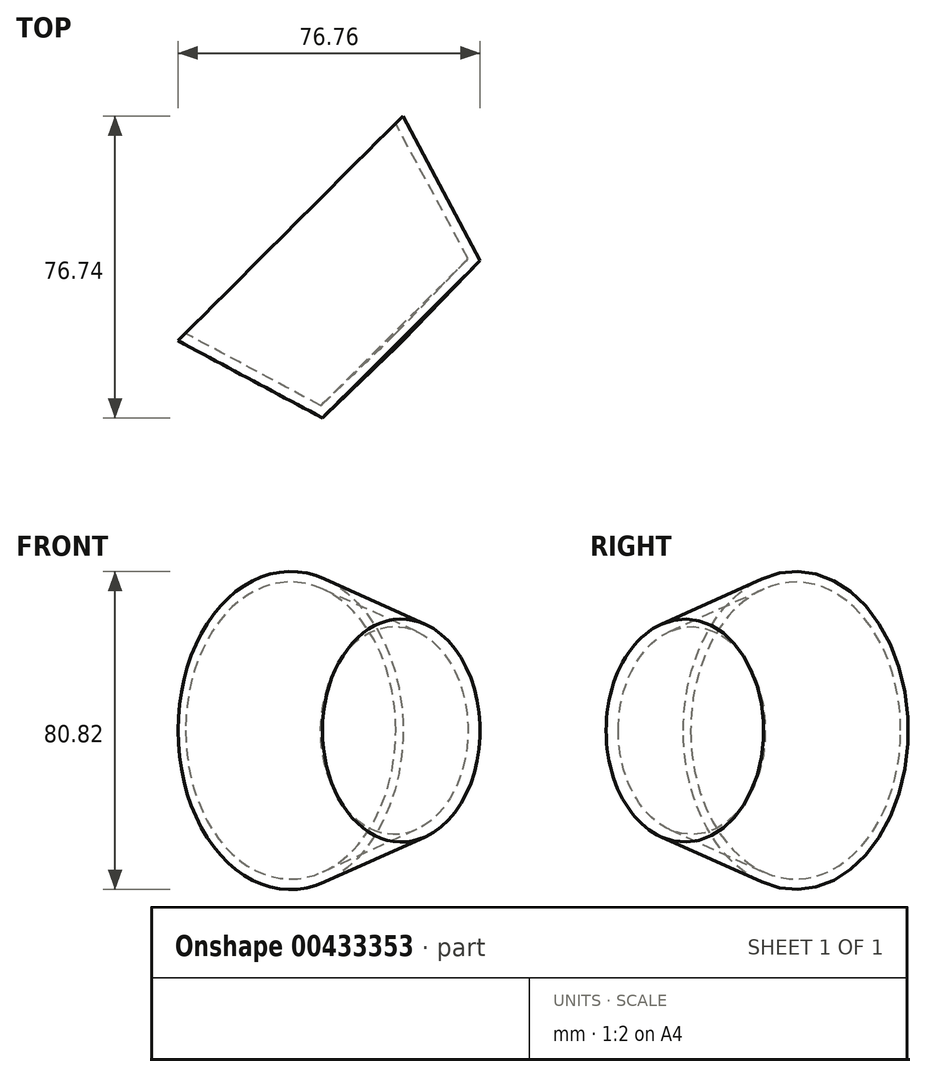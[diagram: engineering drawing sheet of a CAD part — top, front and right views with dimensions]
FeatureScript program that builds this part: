
annotation { "Feature Type Name" : "Feature", "Feature Type Description" : "" }
export const myFeature = defineFeature(function(context is Context, id is Id, definition is map)
    precondition{}
    {
        {
            var Q0;
            Q0=qCreatedBy(makeId("Top.planeOp"),FACE);
            var sketch = newSketch(context, id + "F0", { "sketchPlane" : qUnion([Q0])});
            skLineSegment(sketch, "E0", {"start": v(0, 0) * mm, "end": v(-20.42, -19.63) * mm});
            skLineSegment(sketch, "E1", {"start": v(-20.42, -19.63) * mm, "end": v(-57.11, 0) * mm});
            skLineSegment(sketch, "E2", {"start": v(-57.11, 0) * mm, "end": v(-27.98, 28) * mm});
            skLineSegment(sketch, "E3", {"start": v(-27.98, 28) * mm, "end": v(0, 0) * mm});
            skSolve(sketch);
        }
        {
            var Q0;
            Q0=makeQuery(id+"F0.imprint","IMPRINT",FACE,{"disambiguationData":[TD([[makeQuery(id+"F0.imprint","IMPRINT",EDGE,{"derivedFrom":sQuery(id+"F0.wireOp",EDGE,"E0")}),-1.0]])]});
            var Q1;
            Q1=sQuery(id+"F0.wireOp",EDGE,"E3");
            revolve(context, id + "F1", {"entities" : qUnion([Q0]), "axis" : qUnion([Q1]), "revolveType" : RevolveType.FULL});
        }
        {
            var Q0;
            Q0=makeQuery(id+"F1.opRevolve","SWEPT_FACE",FACE,{"disambiguationData":[OSD([sQuery(id+"F0.wireOp",EDGE,"E2")])]});
            shell(context, id + "F2", {"entities" : qUnion([Q0]), "thickness" : 2.54 * mm});
        }
    });
